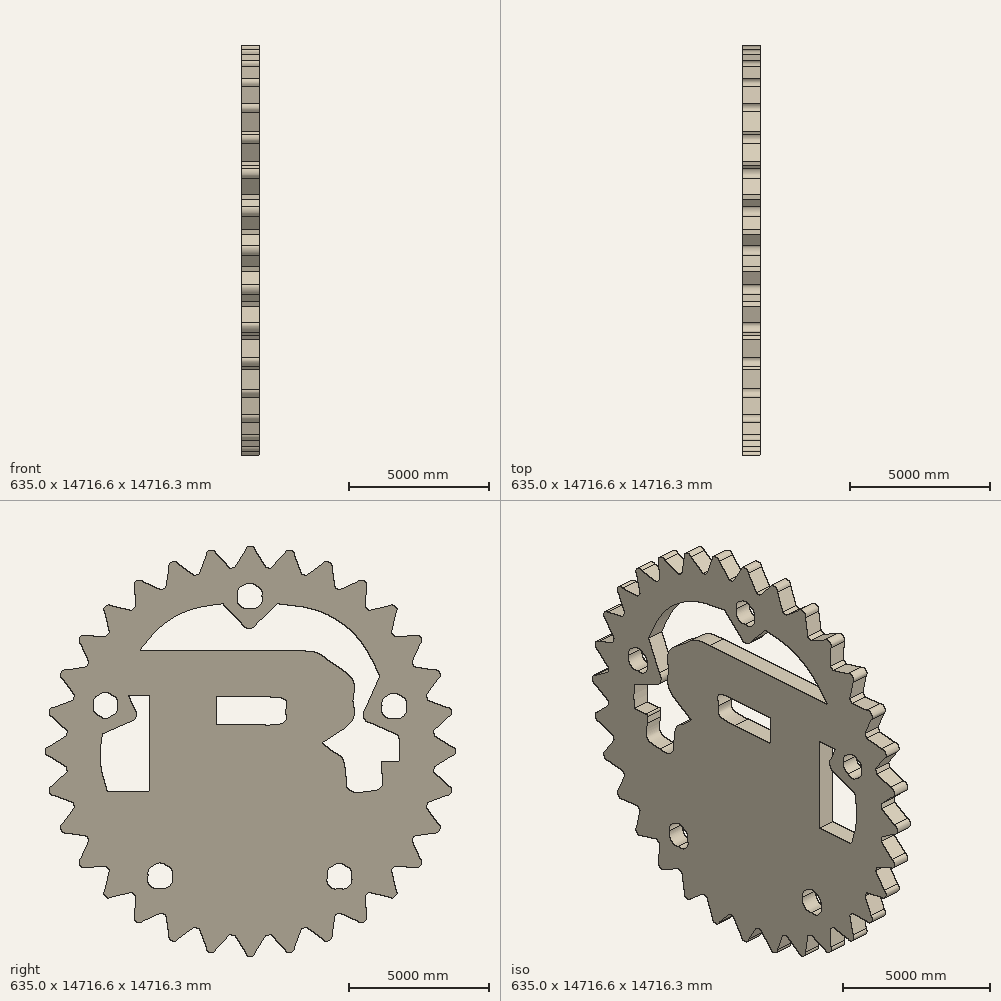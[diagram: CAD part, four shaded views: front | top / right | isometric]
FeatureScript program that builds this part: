
annotation { "Feature Type Name" : "Feature", "Feature Type Description" : "" }
export const myFeature = defineFeature(function(context is Context, id is Id, definition is map)
    precondition{}
    {
        {
            var Q0;
            Q0=qCreatedBy(makeId("Right.planeOp"),FACE);
            var sketch = newSketch(context, id + "F0", { "sketchPlane" : qUnion([Q0])});
            skFitSpline(sketch, "E0", {"points": [v(-456.96, 5582.6) * mm, v(-457.03, 5737.75) * mm, v(-374.3, 5881.15) * mm, v(-239.94, 5958.75) * mm]});
            skFitSpline(sketch, "E1", {"points": [v(-239.94, 5958.75) * mm, v(-105.58, 6036.35) * mm, v(59.97, 6036.35) * mm, v(194.33, 5958.75) * mm]});
            skFitSpline(sketch, "E2", {"points": [v(194.33, 5958.75) * mm, v(328.69, 5881.15) * mm, v(411.42, 5737.75) * mm, v(411.36, 5582.6) * mm]});
            skFitSpline(sketch, "E3", {"points": [v(411.36, 5582.6) * mm, v(411.25, 5342.9) * mm, v(216.9, 5148.63) * mm, v(-22.8, 5148.63) * mm]});
            skFitSpline(sketch, "E4", {"points": [v(-22.8, 5148.63) * mm, v(-262.5, 5148.63) * mm, v(-456.86, 5342.9) * mm, v(-456.96, 5582.6) * mm]});
            skFitSpline(sketch, "E5", {"points": [v(-5636.3, 1651.7) * mm, v(-5636.3, 1806.8) * mm, v(-5553.54, 1950.13) * mm, v(-5419.21, 2027.68) * mm]});
            skFitSpline(sketch, "E6", {"points": [v(-5419.21, 2027.68) * mm, v(-5284.88, 2105.24) * mm, v(-5119.38, 2105.24) * mm, v(-4985.05, 2027.68) * mm]});
            skFitSpline(sketch, "E7", {"points": [v(-4985.05, 2027.68) * mm, v(-4850.72, 1950.13) * mm, v(-4767.97, 1806.8) * mm, v(-4767.97, 1651.7) * mm]});
            skFitSpline(sketch, "E8", {"points": [v(-4767.97, 1651.7) * mm, v(-4767.97, 1496.58) * mm, v(-4850.72, 1353.25) * mm, v(-4985.05, 1275.7) * mm]});
            skFitSpline(sketch, "E9", {"points": [v(-4985.05, 1275.7) * mm, v(-5119.38, 1198.14) * mm, v(-5284.88, 1198.14) * mm, v(-5419.21, 1275.7) * mm]});
            skFitSpline(sketch, "E10", {"points": [v(-5419.21, 1275.7) * mm, v(-5553.54, 1353.25) * mm, v(-5636.3, 1496.58) * mm, v(-5636.3, 1651.7) * mm]});
            skFitSpline(sketch, "E11", {"points": [v(4722.22, 1631.43) * mm, v(4722.16, 1786.6) * mm, v(4804.9, 1929.99) * mm, v(4939.25, 2007.59) * mm]});
            skFitSpline(sketch, "E12", {"points": [v(4939.25, 2007.59) * mm, v(5073.6, 2085.18) * mm, v(5239.16, 2085.18) * mm, v(5373.52, 2007.59) * mm]});
            skFitSpline(sketch, "E13", {"points": [v(5373.52, 2007.59) * mm, v(5507.88, 1929.99) * mm, v(5590.61, 1786.6) * mm, v(5590.54, 1631.43) * mm]});
            skFitSpline(sketch, "E14", {"points": [v(5590.54, 1631.43) * mm, v(5590.44, 1391.73) * mm, v(5396.1, 1197.46) * mm, v(5156.38, 1197.46) * mm]});
            skFitSpline(sketch, "E15", {"points": [v(5156.38, 1197.46) * mm, v(4916.68, 1197.46) * mm, v(4722.33, 1391.73) * mm, v(4722.22, 1631.43) * mm]});
            skFitSpline(sketch, "E16", {"points": [v(-4379.49, 1036.63) * mm, v(-4179.73, 1125.33) * mm, v(-4089.5, 1359.46) * mm, v(-4178.2, 1559.63) * mm]});
            skFitSpline(sketch, "E17", {"points": [v(-3613.28, -1419.42) * mm, v(-3613.28, -1419.42) * mm, v(-5141.64, -1419.42) * mm, v(-5141.64, -1419.42) * mm, v(-3613.28, -1419.42) * mm]});
            skFitSpline(sketch, "E18", {"points": [v(-5141.64, -1419.42) * mm, v(-5330.3, -756.77) * mm, v(-5389.07, -63.9) * mm, v(-5314.72, 621.05) * mm]});
            skLineSegment(sketch, "E19", {"start": v(-4178.2, 1559.63) * mm, "end": v(-4370.83, 1995.2) * mm});
            skLineSegment(sketch, "E20", {"start": v(-4370.83, 1995.2) * mm, "end": v(-3613.28, 1995.2) * mm});
            skLineSegment(sketch, "E21", {"start": v(-3613.28, 1995.2) * mm, "end": v(-3613.28, -1419.42) * mm});
            skLineSegment(sketch, "E22", {"start": v(-4144.46, 1381.72) * mm, "end": v(-4178.2, 1559.63) * mm});
            skLineSegment(sketch, "E23", {"start": v(-5314.72, 621.05) * mm, "end": v(-4379.49, 1036.63) * mm});
            skLineSegment(sketch, "E24", {"start": v(-4379.49, 1036.63) * mm, "end": v(-5314.72, 621.05) * mm});
            skFitSpline(sketch, "E25", {"points": [v(593.37, 1959.15) * mm, v(686.55, 1959.15) * mm, v(1251.32, 1851.45) * mm, v(1251.32, 1429.16) * mm]});
            skFitSpline(sketch, "E26", {"points": [v(1251.32, 1429.16) * mm, v(1251.32, 1078.54) * mm, v(818.14, 952.82) * mm, v(461.92, 952.82) * mm]});
            skLineSegment(sketch, "E27", {"start": v(-1210.6, 952.68) * mm, "end": v(-1210.6, 1959.15) * mm});
            skLineSegment(sketch, "E28", {"start": v(-1210.6, 1959.15) * mm, "end": v(593.37, 1959.15) * mm});
            skFitSpline(sketch, "E29", {"points": [v(-3673.5, -4466.36) * mm, v(-3673.54, -4311.22) * mm, v(-3590.8, -4167.84) * mm, v(-3456.45, -4090.26) * mm]});
            skFitSpline(sketch, "E30", {"points": [v(-3456.45, -4090.26) * mm, v(-3322.1, -4012.67) * mm, v(-3156.56, -4012.67) * mm, v(-3022.21, -4090.26) * mm]});
            skFitSpline(sketch, "E31", {"points": [v(-3022.21, -4090.26) * mm, v(-2887.86, -4167.84) * mm, v(-2805.12, -4311.22) * mm, v(-2805.17, -4466.36) * mm]});
            skFitSpline(sketch, "E32", {"points": [v(-2805.17, -4466.36) * mm, v(-2805.24, -4706.09) * mm, v(-2999.6, -4900.39) * mm, v(-3239.33, -4900.39) * mm]});
            skFitSpline(sketch, "E33", {"points": [v(-3239.33, -4900.39) * mm, v(-3479.06, -4900.39) * mm, v(-3673.42, -4706.09) * mm, v(-3673.5, -4466.36) * mm]});
            skFitSpline(sketch, "E34", {"points": [v(2759.42, -4486.62) * mm, v(2759.32, -4331.44) * mm, v(2842.05, -4188) * mm, v(2976.42, -4110.38) * mm]});
            skFitSpline(sketch, "E35", {"points": [v(2976.42, -4110.38) * mm, v(3110.8, -4032.75) * mm, v(3276.38, -4032.75) * mm, v(3410.75, -4110.38) * mm]});
            skFitSpline(sketch, "E36", {"points": [v(3410.75, -4110.38) * mm, v(3545.12, -4188) * mm, v(3627.85, -4331.44) * mm, v(3627.74, -4486.62) * mm]});
            skFitSpline(sketch, "E37", {"points": [v(3627.74, -4486.62) * mm, v(3627.58, -4726.28) * mm, v(3433.25, -4920.48) * mm, v(3193.58, -4920.48) * mm]});
            skFitSpline(sketch, "E38", {"points": [v(3193.58, -4920.48) * mm, v(2953.92, -4920.48) * mm, v(2759.59, -4726.28) * mm, v(2759.42, -4486.62) * mm]});
            skFitSpline(sketch, "E39", {"points": [v(2893.67, -3502.07) * mm, v(2679.8, -3456.25) * mm, v(2469.43, -3592.31) * mm, v(2423.6, -3806.6) * mm]});
            skFitSpline(sketch, "E40", {"points": [v(2423.6, -3806.6) * mm, v(2423.6, -3806.6) * mm, v(2205.69, -4823.55) * mm, v(2205.69, -4823.55) * mm, v(2423.6, -3806.6) * mm]});
            skFitSpline(sketch, "E41", {"points": [v(2205.69, -4823.55) * mm, v(787.58, -5465.92) * mm, v(-840.11, -5458.11) * mm, v(-2252, -4802.18) * mm]});
            skLineSegment(sketch, "E42", {"start": v(461.92, 952.82) * mm, "end": v(-1210.6, 952.68) * mm});
            skLineSegment(sketch, "E43", {"start": v(-1210.6, 952.68) * mm, "end": v(461.92, 952.82) * mm});
            skFitSpline(sketch, "E44", {"points": [v(-2469.77, -3785.23) * mm, v(-2515.6, -3571.22) * mm, v(-2725.97, -3434.88) * mm, v(-2939.7, -3480.84) * mm]});
            skFitSpline(sketch, "E45", {"points": [v(-2939.7, -3480.84) * mm, v(-2939.7, -3480.84) * mm, v(-3837.49, -3673.61) * mm, v(-3837.49, -3673.61) * mm, v(-2939.7, -3480.84) * mm]});
            skFitSpline(sketch, "E46", {"points": [v(-3837.49, -3673.61) * mm, v(-4004.3, -3501.83) * mm, v(-4159.38, -3319.03) * mm, v(-4301.68, -3126.44) * mm]});
            skLineSegment(sketch, "E47", {"start": v(-2252, -4802.18) * mm, "end": v(-2469.77, -3785.23) * mm});
            skLineSegment(sketch, "E48", {"start": v(-2469.77, -3785.23) * mm, "end": v(-2252, -4802.18) * mm});
            skFitSpline(sketch, "E49", {"points": [v(66.74, -3126.44) * mm, v(116.19, -3126.44) * mm, v(149.16, -3117.5) * mm, v(149.16, -3072.52) * mm]});
            skLineSegment(sketch, "E50", {"start": v(-4301.68, -3126.44) * mm, "end": v(66.74, -3126.44) * mm});
            skLineSegment(sketch, "E51", {"start": v(66.74, -3126.44) * mm, "end": v(-4301.68, -3126.44) * mm});
            skFitSpline(sketch, "E52", {"points": [v(149.16, -1527.26) * mm, v(149.16, -1482.28) * mm, v(116.19, -1473.34) * mm, v(66.74, -1473.34) * mm]});
            skLineSegment(sketch, "E53", {"start": v(149.16, -3072.52) * mm, "end": v(149.16, -1527.26) * mm});
            skLineSegment(sketch, "E54", {"start": v(149.16, -1527.26) * mm, "end": v(149.16, -3072.52) * mm});
            skFitSpline(sketch, "E55", {"points": [v(170.95, -493.83) * mm, v(297.09, -493.83) * mm, v(845.38, -529.87) * mm, v(1020.69, -1230.7) * mm]});
            skFitSpline(sketch, "E56", {"points": [v(1020.69, -1230.7) * mm, v(1075.59, -1446.24) * mm, v(1196.14, -2147.35) * mm, v(1278.56, -2371.83) * mm]});
            skFitSpline(sketch, "E57", {"points": [v(1278.56, -2371.83) * mm, v(1360.7, -2623.56) * mm, v(1695.12, -3126.44) * mm, v(2051.47, -3126.44) * mm]});
            skLineSegment(sketch, "E58", {"start": v(66.74, -1473.34) * mm, "end": v(-1210.88, -1473.34) * mm});
            skLineSegment(sketch, "E59", {"start": v(-1210.88, -1473.34) * mm, "end": v(-1210.88, -493.83) * mm});
            skLineSegment(sketch, "E60", {"start": v(-1210.88, -493.83) * mm, "end": v(170.95, -493.83) * mm});
            skFitSpline(sketch, "E61", {"points": [v(4306.92, -3126.44) * mm, v(4155.65, -3328.91) * mm, v(3990.22, -3520.4) * mm, v(3811.86, -3699.46) * mm]});
            skLineSegment(sketch, "E62", {"start": v(2051.47, -3126.44) * mm, "end": v(4306.92, -3126.44) * mm});
            skLineSegment(sketch, "E63", {"start": v(4306.92, -3126.44) * mm, "end": v(2051.47, -3126.44) * mm});
            skFitSpline(sketch, "E64", {"points": [v(5319.4, 577.88) * mm, v(5350.07, 269.48) * mm, v(5353.86, -41.02) * mm, v(5330.72, -350.08) * mm]});
            skLineSegment(sketch, "E65", {"start": v(3811.86, -3699.46) * mm, "end": v(2893.67, -3502.07) * mm});
            skLineSegment(sketch, "E66", {"start": v(2893.67, -3502.07) * mm, "end": v(3811.86, -3699.46) * mm});
            skFitSpline(sketch, "E67", {"points": [v(4782.3, -350.08) * mm, v(4727.4, -350.08) * mm, v(4705.32, -386.12) * mm, v(4705.32, -439.9) * mm]});
            skLineSegment(sketch, "E68", {"start": v(5330.72, -350.08) * mm, "end": v(4782.3, -350.08) * mm});
            skLineSegment(sketch, "E69", {"start": v(4782.3, -350.08) * mm, "end": v(5330.72, -350.08) * mm});
            skFitSpline(sketch, "E70", {"points": [v(4705.32, -691.77) * mm, v(4705.32, -1284.62) * mm, v(4371.04, -1413.55) * mm, v(4078.1, -1446.38) * mm]});
            skFitSpline(sketch, "E71", {"points": [v(4078.1, -1446.38) * mm, v(3799.15, -1477.8) * mm, v(3489.87, -1329.6) * mm, v(3451.73, -1158.9) * mm]});
            skFitSpline(sketch, "E72", {"points": [v(3451.73, -1158.9) * mm, v(3287.18, -233.3) * mm, v(3012.96, -35.64) * mm, v(2579.92, 305.9) * mm]});
            skFitSpline(sketch, "E73", {"points": [v(2579.92, 305.9) * mm, v(3117.31, 647.17) * mm, v(3676.5, 1150.62) * mm, v(3676.5, 1824.49) * mm]});
            skFitSpline(sketch, "E74", {"points": [v(3676.5, 1824.49) * mm, v(3676.5, 2552.14) * mm, v(3177.66, 3010.47) * mm, v(2837.65, 3235.23) * mm]});
            skFitSpline(sketch, "E75", {"points": [v(2837.65, 3235.23) * mm, v(2360.6, 3549.67) * mm, v(1832.43, 3612.67) * mm, v(1689.95, 3612.67) * mm]});
            skFitSpline(sketch, "E76", {"points": [v(1689.95, 3612.67) * mm, v(1689.95, 3612.67) * mm, v(-3981.93, 3612.67) * mm, v(-3981.93, 3612.67) * mm, v(1689.95, 3612.67) * mm]});
            skFitSpline(sketch, "E77", {"points": [v(-3981.93, 3612.67) * mm, v(-3197.85, 4488.85) * mm, v(-2146.75, 5082.06) * mm, v(-991.42, 5300.42) * mm]});
            skLineSegment(sketch, "E78", {"start": v(4705.32, -439.9) * mm, "end": v(4705.32, -691.77) * mm});
            skLineSegment(sketch, "E79", {"start": v(4705.32, -691.77) * mm, "end": v(4705.32, -439.9) * mm});
            skFitSpline(sketch, "E80", {"points": [v(-322.86, 4599.03) * mm, v(-171.71, 4440.76) * mm, v(78.61, 4434.9) * mm, v(236.74, 4586.18) * mm]});
            skLineSegment(sketch, "E81", {"start": v(-991.42, 5300.42) * mm, "end": v(-322.86, 4599.03) * mm});
            skLineSegment(sketch, "E82", {"start": v(-322.86, 4599.03) * mm, "end": v(-991.42, 5300.42) * mm});
            skFitSpline(sketch, "E83", {"points": [v(984.79, 5301.68) * mm, v(2528.16, 5012.59) * mm, v(3866.36, 4059.51) * mm, v(4644.14, 2695.46) * mm]});
            skLineSegment(sketch, "E84", {"start": v(236.74, 4586.18) * mm, "end": v(984.79, 5301.68) * mm});
            skLineSegment(sketch, "E85", {"start": v(984.79, 5301.68) * mm, "end": v(236.74, 4586.18) * mm});
            skFitSpline(sketch, "E86", {"points": [v(4132.03, 1538.82) * mm, v(4043.6, 1338.64) * mm, v(4133.84, 1104.52) * mm, v(4333.46, 1015.82) * mm]});
            skLineSegment(sketch, "E87", {"start": v(4644.14, 2695.46) * mm, "end": v(4132.03, 1538.82) * mm});
            skLineSegment(sketch, "E88", {"start": v(4132.03, 1538.82) * mm, "end": v(4644.14, 2695.46) * mm});
            skLineSegment(sketch, "E89", {"start": v(4333.46, 1015.82) * mm, "end": v(5319.4, 577.88) * mm});
            skLineSegment(sketch, "E90", {"start": v(5319.4, 577.88) * mm, "end": v(4333.46, 1015.82) * mm});
            skFitSpline(sketch, "E91", {"points": [v(7106.61, 1229.96) * mm, v(7213.9, 1329.98) * mm, v(7173.8, 1531.28) * mm, v(7036.63, 1582.4) * mm]});
            skLineSegment(sketch, "E92", {"start": v(6596.6, 559.17) * mm, "end": v(6579.14, 737.97) * mm});
            skLineSegment(sketch, "E93", {"start": v(6579.14, 737.97) * mm, "end": v(7106.61, 1229.96) * mm});
            skLineSegment(sketch, "E94", {"start": v(7106.61, 1229.96) * mm, "end": v(6596.6, 559.17) * mm});
            skFitSpline(sketch, "E95", {"points": [v(6730.14, 2592.79) * mm, v(6815.91, 2711.53) * mm, v(6737.13, 2901.09) * mm, v(6592.69, 2924.83) * mm]});
            skLineSegment(sketch, "E96", {"start": v(7036.63, 1582.4) * mm, "end": v(6362.34, 1834.55) * mm});
            skLineSegment(sketch, "E97", {"start": v(6362.34, 1834.55) * mm, "end": v(6309.53, 2008.6) * mm});
            skLineSegment(sketch, "E98", {"start": v(6309.53, 2008.6) * mm, "end": v(6730.14, 2592.79) * mm});
            skFitSpline(sketch, "E99", {"points": [v(6094.97, 3856.02) * mm, v(6156.15, 3989.56) * mm, v(6042.44, 4160.4) * mm, v(5895.49, 4154.82) * mm]});
            skLineSegment(sketch, "E100", {"start": v(6592.69, 2924.83) * mm, "end": v(5881.66, 3040.5) * mm});
            skLineSegment(sketch, "E101", {"start": v(5881.66, 3040.5) * mm, "end": v(5796.17, 3200.17) * mm});
            skLineSegment(sketch, "E102", {"start": v(5796.17, 3200.17) * mm, "end": v(6094.97, 3856.02) * mm});
            skFitSpline(sketch, "E103", {"points": [v(5225.67, 4970.9) * mm, v(5259.2, 5113.66) * mm, v(5114.34, 5258.65) * mm, v(4971.57, 5225.13) * mm]});
            skLineSegment(sketch, "E104", {"start": v(5895.49, 4154.82) * mm, "end": v(5173.85, 4129.67) * mm});
            skLineSegment(sketch, "E105", {"start": v(5173.85, 4129.67) * mm, "end": v(5059.86, 4267.97) * mm});
            skLineSegment(sketch, "E106", {"start": v(5059.86, 4267.97) * mm, "end": v(5225.67, 4970.9) * mm});
            skFitSpline(sketch, "E107", {"points": [v(4155.5, 5895.09) * mm, v(4161.08, 6041.2) * mm, v(3990.1, 6155.33) * mm, v(3856.84, 6094.7) * mm]});
            skLineSegment(sketch, "E108", {"start": v(4971.57, 5225.13) * mm, "end": v(4268.79, 5059.45) * mm});
            skLineSegment(sketch, "E109", {"start": v(4268.79, 5059.45) * mm, "end": v(4130.21, 5173.44) * mm});
            skLineSegment(sketch, "E110", {"start": v(4130.21, 5173.44) * mm, "end": v(4155.5, 5895.09) * mm});
            skFitSpline(sketch, "E111", {"points": [v(2925.52, 6592.56) * mm, v(2902.05, 6736.73) * mm, v(2712.35, 6815.51) * mm, v(2593.61, 6730.02) * mm]});
            skLineSegment(sketch, "E112", {"start": v(3856.84, 6094.7) * mm, "end": v(3201.13, 5795.77) * mm});
            skLineSegment(sketch, "E113", {"start": v(3201.13, 5795.77) * mm, "end": v(3041.46, 5881.4) * mm});
            skLineSegment(sketch, "E114", {"start": v(3041.46, 5881.4) * mm, "end": v(2925.52, 6592.56) * mm});
            skFitSpline(sketch, "E115", {"points": [v(1583.09, 7036.5) * mm, v(1531.96, 7173.96) * mm, v(1330.52, 7213.5) * mm, v(1230.78, 7106.77) * mm]});
            skLineSegment(sketch, "E116", {"start": v(2593.61, 6730.02) * mm, "end": v(2009, 6309.41) * mm});
            skLineSegment(sketch, "E117", {"start": v(2009, 6309.41) * mm, "end": v(1835.23, 6362.07) * mm});
            skLineSegment(sketch, "E118", {"start": v(1835.23, 6362.07) * mm, "end": v(1583.09, 7036.5) * mm});
            skFitSpline(sketch, "E119", {"points": [v(180.03, 7210.28) * mm, v(103.2, 7334.6) * mm, v(-102.57, 7334.6) * mm, v(-179.12, 7210.28) * mm]});
            skLineSegment(sketch, "E120", {"start": v(1230.78, 7106.77) * mm, "end": v(738.8, 6578.87) * mm});
            skLineSegment(sketch, "E121", {"start": v(738.8, 6578.87) * mm, "end": v(559.99, 6596.34) * mm});
            skLineSegment(sketch, "E122", {"start": v(559.99, 6596.34) * mm, "end": v(180.03, 7210.28) * mm});
            skFitSpline(sketch, "E123", {"points": [v(-1230.15, 7106.77) * mm, v(-1329.9, 7213.5) * mm, v(-1531.33, 7173.96) * mm, v(-1582.45, 7036.5) * mm]});
            skLineSegment(sketch, "E124", {"start": v(-179.12, 7210.28) * mm, "end": v(-559.08, 6596.34) * mm});
            skLineSegment(sketch, "E125", {"start": v(-559.08, 6596.34) * mm, "end": v(-738.02, 6578.87) * mm});
            skLineSegment(sketch, "E126", {"start": v(-738.02, 6578.87) * mm, "end": v(-1230.15, 7106.77) * mm});
            skFitSpline(sketch, "E127", {"points": [v(-2592.98, 6730.02) * mm, v(-2711.72, 6815.8) * mm, v(-2901.56, 6736.73) * mm, v(-2925.03, 6592.56) * mm]});
            skLineSegment(sketch, "E128", {"start": v(-1582.45, 7036.5) * mm, "end": v(-1834.6, 6362.07) * mm});
            skLineSegment(sketch, "E129", {"start": v(-1834.6, 6362.07) * mm, "end": v(-2008.51, 6309.41) * mm});
            skLineSegment(sketch, "E130", {"start": v(-2008.51, 6309.41) * mm, "end": v(-2592.98, 6730.02) * mm});
            skFitSpline(sketch, "E131", {"points": [v(-3856.35, 6094.7) * mm, v(-3989.61, 6155.61) * mm, v(-4160.6, 6041.2) * mm, v(-4155, 5895.09) * mm]});
            skLineSegment(sketch, "E132", {"start": v(-2925.03, 6592.56) * mm, "end": v(-3040.97, 5881.4) * mm});
            skLineSegment(sketch, "E133", {"start": v(-3040.97, 5881.4) * mm, "end": v(-3200.64, 5795.77) * mm});
            skLineSegment(sketch, "E134", {"start": v(-3200.64, 5795.77) * mm, "end": v(-3856.35, 6094.7) * mm});
            skFitSpline(sketch, "E135", {"points": [v(-4971.22, 5225.13) * mm, v(-5113.99, 5258.38) * mm, v(-5258.98, 5113.66) * mm, v(-5225.46, 4970.9) * mm]});
            skLineSegment(sketch, "E136", {"start": v(-4155, 5895.09) * mm, "end": v(-4129.86, 5173.44) * mm});
            skLineSegment(sketch, "E137", {"start": v(-4129.86, 5173.44) * mm, "end": v(-4268.44, 5059.45) * mm});
            skLineSegment(sketch, "E138", {"start": v(-4268.44, 5059.45) * mm, "end": v(-4971.22, 5225.13) * mm});
            skFitSpline(sketch, "E139", {"points": [v(-5895.28, 4154.82) * mm, v(-6040.84, 4159) * mm, v(-6155.52, 3989.56) * mm, v(-6094.9, 3856.02) * mm]});
            skLineSegment(sketch, "E140", {"start": v(-5225.46, 4970.9) * mm, "end": v(-5059.93, 4267.97) * mm});
            skLineSegment(sketch, "E141", {"start": v(-5059.93, 4267.97) * mm, "end": v(-5173.63, 4129.67) * mm});
            skLineSegment(sketch, "E142", {"start": v(-5173.63, 4129.67) * mm, "end": v(-5895.28, 4154.82) * mm});
            skFitSpline(sketch, "E143", {"points": [v(-6592.62, 2924.83) * mm, v(-6737.06, 2901.37) * mm, v(-6815.28, 2711.53) * mm, v(-6730.07, 2592.79) * mm]});
            skLineSegment(sketch, "E144", {"start": v(-6094.9, 3856.02) * mm, "end": v(-5795.96, 3200.17) * mm});
            skLineSegment(sketch, "E145", {"start": v(-5795.96, 3200.17) * mm, "end": v(-5881.59, 3040.5) * mm});
            skLineSegment(sketch, "E146", {"start": v(-5881.59, 3040.5) * mm, "end": v(-6592.62, 2924.83) * mm});
            skFitSpline(sketch, "E147", {"points": [v(-7036.7, 1582.4) * mm, v(-7173.6, 1531.28) * mm, v(-7213.68, 1329.98) * mm, v(-7106.68, 1229.96) * mm]});
            skLineSegment(sketch, "E148", {"start": v(-6730.07, 2592.79) * mm, "end": v(-6309.46, 2008.6) * mm});
            skLineSegment(sketch, "E149", {"start": v(-6309.46, 2008.6) * mm, "end": v(-6362.27, 1834.55) * mm});
            skLineSegment(sketch, "E150", {"start": v(-6362.27, 1834.55) * mm, "end": v(-7036.7, 1582.4) * mm});
            skFitSpline(sketch, "E151", {"points": [v(-7210.33, 179.2) * mm, v(-7334.66, 102.38) * mm, v(-7334.66, -103.39) * mm, v(-7210.33, -179.94) * mm]});
            skLineSegment(sketch, "E152", {"start": v(-7106.68, 1229.96) * mm, "end": v(-6579.07, 737.97) * mm});
            skLineSegment(sketch, "E153", {"start": v(-6579.07, 737.97) * mm, "end": v(-6596.53, 559.17) * mm});
            skLineSegment(sketch, "E154", {"start": v(-6596.53, 559.17) * mm, "end": v(-7210.33, 179.2) * mm});
            skFitSpline(sketch, "E155", {"points": [v(-7106.68, -1230.84) * mm, v(-7213.68, -1330.58) * mm, v(-7173.6, -1531.73) * mm, v(-7036.7, -1583.14) * mm]});
            skLineSegment(sketch, "E156", {"start": v(-7210.33, -179.94) * mm, "end": v(-6596.53, -559.9) * mm});
            skLineSegment(sketch, "E157", {"start": v(-6596.53, -559.9) * mm, "end": v(-6579.07, -738.7) * mm});
            skLineSegment(sketch, "E158", {"start": v(-6579.07, -738.7) * mm, "end": v(-7106.68, -1230.84) * mm});
            skFitSpline(sketch, "E159", {"points": [v(-6730.07, -2593.66) * mm, v(-6815.56, -2712.68) * mm, v(-6736.92, -2902.38) * mm, v(-6592.48, -2925.57) * mm]});
            skLineSegment(sketch, "E160", {"start": v(-7036.7, -1583.14) * mm, "end": v(-6362.27, -1835.28) * mm});
            skLineSegment(sketch, "E161", {"start": v(-6362.27, -1835.28) * mm, "end": v(-6309.46, -2009.33) * mm});
            skLineSegment(sketch, "E162", {"start": v(-6309.46, -2009.33) * mm, "end": v(-6730.07, -2593.66) * mm});
            skFitSpline(sketch, "E163", {"points": [v(-6094.9, -3856.75) * mm, v(-6155.8, -3990.01) * mm, v(-6040.84, -4161.42) * mm, v(-5895.28, -4155.55) * mm]});
            skLineSegment(sketch, "E164", {"start": v(-6592.48, -2925.57) * mm, "end": v(-5881.59, -3041.23) * mm});
            skLineSegment(sketch, "E165", {"start": v(-5881.59, -3041.23) * mm, "end": v(-5795.96, -3201.18) * mm});
            skLineSegment(sketch, "E166", {"start": v(-5795.96, -3201.18) * mm, "end": v(-6094.9, -3856.75) * mm});
            skFitSpline(sketch, "E167", {"points": [v(-5225.46, -4971.9) * mm, v(-5258.98, -5114.39) * mm, v(-5113.99, -5259.1) * mm, v(-4971.22, -5225.58) * mm]});
            skLineSegment(sketch, "E168", {"start": v(-5895.28, -4155.55) * mm, "end": v(-5173.91, -4130.26) * mm});
            skLineSegment(sketch, "E169", {"start": v(-5173.91, -4130.26) * mm, "end": v(-5059.93, -4268.84) * mm});
            skLineSegment(sketch, "E170", {"start": v(-5059.93, -4268.84) * mm, "end": v(-5225.46, -4971.9) * mm});
            skFitSpline(sketch, "E171", {"points": [v(-4155, -5895.54) * mm, v(-4160.6, -6041.66) * mm, v(-3989.61, -6155.93) * mm, v(-3856.35, -6095.02) * mm]});
            skLineSegment(sketch, "E172", {"start": v(-4971.22, -5225.58) * mm, "end": v(-4268.44, -5060.05) * mm});
            skLineSegment(sketch, "E173", {"start": v(-4268.44, -5060.05) * mm, "end": v(-4129.86, -5173.76) * mm});
            skLineSegment(sketch, "E174", {"start": v(-4129.86, -5173.76) * mm, "end": v(-4155, -5895.54) * mm});
            skFitSpline(sketch, "E175", {"points": [v(-2925.03, -6592.6) * mm, v(-2901.56, -6737.32) * mm, v(-2711.72, -6815.55) * mm, v(-2592.98, -6730.34) * mm]});
            skLineSegment(sketch, "E176", {"start": v(-3856.35, -6095.02) * mm, "end": v(-3200.64, -5796.22) * mm});
            skLineSegment(sketch, "E177", {"start": v(-3200.64, -5796.22) * mm, "end": v(-3040.97, -5881.85) * mm});
            skLineSegment(sketch, "E178", {"start": v(-3040.97, -5881.85) * mm, "end": v(-2925.03, -6592.6) * mm});
            skFitSpline(sketch, "E179", {"points": [v(-1582.6, -7036.54) * mm, v(-1531.47, -7173.44) * mm, v(-1330.03, -7213.8) * mm, v(-1230.3, -7106.52) * mm]});
            skLineSegment(sketch, "E180", {"start": v(-2592.98, -6730.34) * mm, "end": v(-2008.8, -6309.45) * mm});
            skLineSegment(sketch, "E181", {"start": v(-2008.8, -6309.45) * mm, "end": v(-1834.74, -6362.39) * mm});
            skLineSegment(sketch, "E182", {"start": v(-1834.74, -6362.39) * mm, "end": v(-1582.6, -7036.54) * mm});
            skFitSpline(sketch, "E183", {"points": [v(-179.26, -7210.6) * mm, v(-102.7, -7334.36) * mm, v(103.06, -7334.64) * mm, v(179.89, -7210.6) * mm]});
            skLineSegment(sketch, "E184", {"start": v(-1230.3, -7106.52) * mm, "end": v(-738.16, -6578.9) * mm});
            skLineSegment(sketch, "E185", {"start": v(-738.16, -6578.9) * mm, "end": v(-559.22, -6596.8) * mm});
            skLineSegment(sketch, "E186", {"start": v(-559.22, -6596.8) * mm, "end": v(-179.26, -7210.6) * mm});
            skFitSpline(sketch, "E187", {"points": [v(1230.64, -7106.52) * mm, v(1330.38, -7213.8) * mm, v(1531.82, -7173.44) * mm, v(1582.95, -7036.54) * mm]});
            skLineSegment(sketch, "E188", {"start": v(179.89, -7210.6) * mm, "end": v(559.85, -6596.8) * mm});
            skLineSegment(sketch, "E189", {"start": v(559.85, -6596.8) * mm, "end": v(738.65, -6578.9) * mm});
            skLineSegment(sketch, "E190", {"start": v(738.65, -6578.9) * mm, "end": v(1230.64, -7106.52) * mm});
            skFitSpline(sketch, "E191", {"points": [v(2593.47, -6730.34) * mm, v(2712.2, -6815.55) * mm, v(2901.9, -6737.04) * mm, v(2925.38, -6592.6) * mm]});
            skLineSegment(sketch, "E192", {"start": v(1582.95, -7036.54) * mm, "end": v(1835.09, -6362.39) * mm});
            skLineSegment(sketch, "E193", {"start": v(1835.09, -6362.39) * mm, "end": v(2009.14, -6309.45) * mm});
            skLineSegment(sketch, "E194", {"start": v(2009.14, -6309.45) * mm, "end": v(2593.47, -6730.34) * mm});
            skFitSpline(sketch, "E195", {"points": [v(3856.7, -6095.02) * mm, v(3989.96, -6155.93) * mm, v(4160.67, -6041.94) * mm, v(4155.36, -5895.54) * mm]});
            skLineSegment(sketch, "E196", {"start": v(2925.38, -6592.6) * mm, "end": v(3041.32, -5881.85) * mm});
            skLineSegment(sketch, "E197", {"start": v(3041.32, -5881.85) * mm, "end": v(3200.99, -5796.22) * mm});
            skLineSegment(sketch, "E198", {"start": v(3200.99, -5796.22) * mm, "end": v(3856.7, -6095.02) * mm});
            skFitSpline(sketch, "E199", {"points": [v(4971.43, -5225.58) * mm, v(5114.2, -5259.1) * mm, v(5259.06, -5114.39) * mm, v(5225.53, -4971.9) * mm]});
            skLineSegment(sketch, "E200", {"start": v(4155.36, -5895.54) * mm, "end": v(4130.21, -5173.76) * mm});
            skLineSegment(sketch, "E201", {"start": v(4130.21, -5173.76) * mm, "end": v(4268.65, -5060.05) * mm});
            skLineSegment(sketch, "E202", {"start": v(4268.65, -5060.05) * mm, "end": v(4971.43, -5225.58) * mm});
            skFitSpline(sketch, "E203", {"points": [v(5895.35, -4155.55) * mm, v(6040.9, -4161.42) * mm, v(6156.01, -3990.01) * mm, v(6094.83, -3856.75) * mm]});
            skLineSegment(sketch, "E204", {"start": v(5225.53, -4971.9) * mm, "end": v(5060, -4268.84) * mm});
            skLineSegment(sketch, "E205", {"start": v(5060, -4268.84) * mm, "end": v(5173.7, -4130.26) * mm});
            skLineSegment(sketch, "E206", {"start": v(5173.7, -4130.26) * mm, "end": v(5895.35, -4155.55) * mm});
            skFitSpline(sketch, "E207", {"points": [v(6592.55, -2925.57) * mm, v(6737.27, -2902.38) * mm, v(6815.77, -2712.68) * mm, v(6730, -2593.66) * mm]});
            skLineSegment(sketch, "E208", {"start": v(6094.83, -3856.75) * mm, "end": v(5796.03, -3201.18) * mm});
            skLineSegment(sketch, "E209", {"start": v(5796.03, -3201.18) * mm, "end": v(5881.52, -3041.23) * mm});
            skLineSegment(sketch, "E210", {"start": v(5881.52, -3041.23) * mm, "end": v(6592.55, -2925.57) * mm});
            skFitSpline(sketch, "E211", {"points": [v(7036.49, -1583.14) * mm, v(7173.66, -1531.73) * mm, v(7213.75, -1330.58) * mm, v(7106.47, -1230.84) * mm]});
            skLineSegment(sketch, "E212", {"start": v(6730, -2593.66) * mm, "end": v(6309.4, -2009.33) * mm});
            skLineSegment(sketch, "E213", {"start": v(6309.4, -2009.33) * mm, "end": v(6362.2, -1835.28) * mm});
            skLineSegment(sketch, "E214", {"start": v(6362.2, -1835.28) * mm, "end": v(7036.49, -1583.14) * mm});
            skFitSpline(sketch, "E215", {"points": [v(7210.26, -179.94) * mm, v(7334.59, -103.39) * mm, v(7334.73, 102.38) * mm, v(7210.38, 179.2) * mm]});
            skLineSegment(sketch, "E216", {"start": v(7106.47, -1230.84) * mm, "end": v(6579, -738.7) * mm});
            skLineSegment(sketch, "E217", {"start": v(6579, -738.7) * mm, "end": v(6596.46, -559.9) * mm});
            skLineSegment(sketch, "E218", {"start": v(6596.46, -559.9) * mm, "end": v(7210.26, -179.94) * mm});
            skLineSegment(sketch, "E219", {"start": v(7210.38, 179.2) * mm, "end": v(6596.6, 559.17) * mm});
            skLineSegment(sketch, "E220", {"start": v(6596.6, 559.17) * mm, "end": v(7210.38, 179.2) * mm});
            skLineSegment(sketch, "E221", {"start": v(-5141.64, -1419.42) * mm, "end": v(-3613.28, -1419.42) * mm});
            skSolve(sketch);
        }
        {
            var Q0;
            Q0=makeQuery(id+"F0.imprint","IMPRINT",FACE,{"disambiguationData":[TD([[makeQuery(id+"F0.imprint","IMPRINT",EDGE,{"derivedFrom":sQuery(id+"F0.wireOp",EDGE,"E0")}),1.0]])]});
            extrude(context, id + "F1", {"entities" : qUnion([Q0]), "depth" : 635 * mm});
        }
    });
